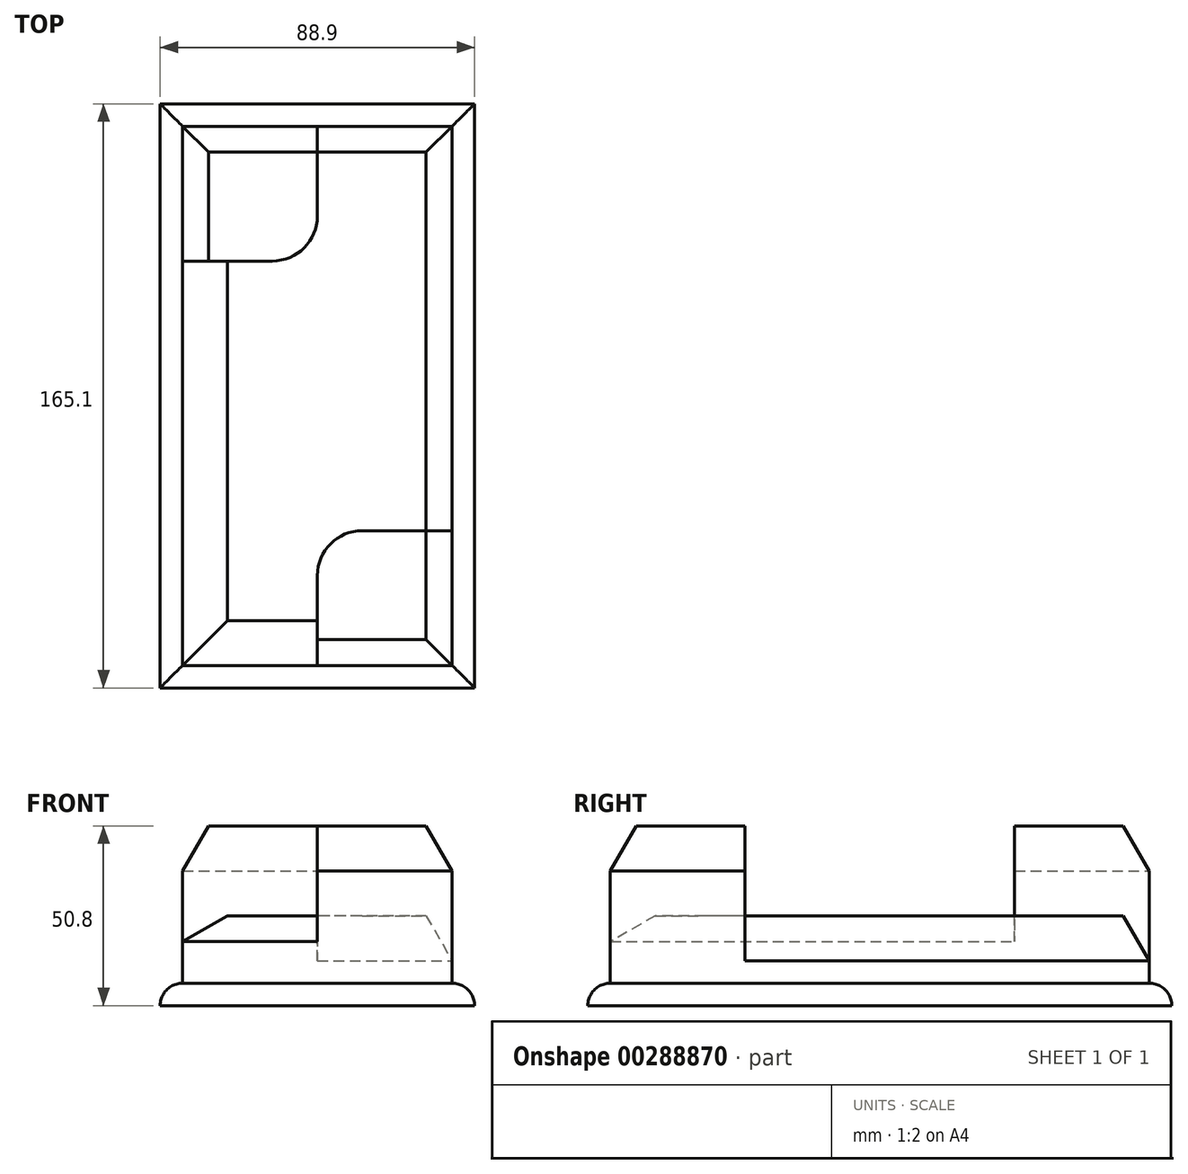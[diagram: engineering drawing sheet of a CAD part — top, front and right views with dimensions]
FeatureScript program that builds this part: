
annotation { "Feature Type Name" : "Feature", "Feature Type Description" : "" }
export const myFeature = defineFeature(function(context is Context, id is Id, definition is map)
    precondition{}
    {
        {
            var Q0;
            Q0=qCreatedBy(makeId("Top.planeOp"),FACE);
            var sketch = newSketch(context, id + "F0", { "sketchPlane" : qUnion([Q0])});
            skLineSegment(sketch, "E0.bottom", {"start": v(-58.88, 81.26) * mm, "end": v(30.02, 81.26) * mm});
            skLineSegment(sketch, "E0.top", {"start": v(-58.88, -83.84) * mm, "end": v(30.02, -83.84) * mm});
            skLineSegment(sketch, "E0.left", {"start": v(-58.88, 81.26) * mm, "end": v(-58.88, -83.84) * mm});
            skLineSegment(sketch, "E0.right", {"start": v(30.02, 81.26) * mm, "end": v(30.02, -83.84) * mm});
            skLineSegment(sketch, "E1.0", {"start": v(-52.53, 74.91) * mm, "end": v(23.67, 74.91) * mm});
            skLineSegment(sketch, "E1.1", {"start": v(-52.53, 74.91) * mm, "end": v(-52.53, -77.49) * mm});
            skLineSegment(sketch, "E1.2", {"start": v(-52.53, -77.49) * mm, "end": v(23.67, -77.49) * mm});
            skLineSegment(sketch, "E1.3", {"start": v(23.67, 74.91) * mm, "end": v(23.67, -77.49) * mm});
            skLineSegment(sketch, "E2", {"start": v(-14.43, 74.91) * mm, "end": v(-14.43, 49.51) * mm});
            skLineSegment(sketch, "E3", {"start": v(-27.13, 36.81) * mm, "end": v(-52.53, 36.81) * mm});
            skLineSegment(sketch, "E4", {"start": v(-14.43, -77.49) * mm, "end": v(-14.43, -52.09) * mm});
            skLineSegment(sketch, "E5", {"start": v(-1.73, -39.39) * mm, "end": v(23.67, -39.39) * mm});
            skPoint(sketch, "E6.visualSharp", {"position": v(-14.43, 36.81) * mm});
            skArc(sketch, "E6.filletArc", {"start": v(-27.13, 36.81) * mm, "mid": v(-18.15, 40.53) * mm, "end": v(-14.43, 49.51) * mm});
            skPoint(sketch, "E7.visualSharp", {"position": v(-14.43, -39.39) * mm});
            skArc(sketch, "E7.filletArc", {"start": v(-1.73, -39.39) * mm, "mid": v(-10.71, -43.1) * mm, "end": v(-14.43, -52.09) * mm});
            skSolve(sketch);
        }
        {
            var Q0;
            Q0=makeQuery(id+"F0.imprint","IMPRINT",FACE,{"disambiguationData":[TD([[makeQuery(id+"F0.imprint","IMPRINT",EDGE,{"derivedFrom":sQuery(id+"F0.wireOp",EDGE,"E0.bottom")}),-1.0]])]});
            extrude(context, id + "F1", {"entities" : qUnion([Q0]), "depth" : 6.35 * mm});
        }
        {
            var Q0;
            {var subQ9=sQuery(id+"F0.wireOp",EDGE,"E2");Q0=makeQuery(id+"F0.imprint","IMPRINT",FACE,{"disambiguationData":[TD([[makeQuery(id+"F0.imprint","IMPRINT",EDGE,{"derivedFrom":subQ9}),1.0]])]});}
            extrude(context, id + "F2", {"entities" : qUnion([Q0]), "operationType" : NewBodyOperationType.ADD, "depth" : 25.4 * mm});
        }
        {
            var Q0;
            {var subQ1=sQuery(id+"F0.wireOp",EDGE,"E2");Q0=makeQuery(id+"F0.imprint","IMPRINT",FACE,{"disambiguationData":[TD([[makeQuery(id+"F0.imprint","IMPRINT",EDGE,{"derivedFrom":subQ1}),-1.0]])]});}
            var Q1;
            {var subQ4=sQuery(id+"F0.wireOp",EDGE,"E4");Q1=makeQuery(id+"F0.imprint","IMPRINT",FACE,{"disambiguationData":[TD([[makeQuery(id+"F0.imprint","IMPRINT",EDGE,{"derivedFrom":subQ4}),-1.0]])]});}
            extrude(context, id + "F3", {"entities" : qUnion([Q0, Q1]), "operationType" : NewBodyOperationType.ADD, "depth" : 50.8 * mm});
        }
        {
            var Q0;
            Q0=makeQuery(id+"F1.opExtrude","CAP_EDGE",EDGE,{"disambiguationData":[OSD([sQuery(id+"F0.wireOp",EDGE,"E0.top")])],"isStart":false});
            var Q1;
            Q1=makeQuery(id+"F1.opExtrude","CAP_EDGE",EDGE,{"disambiguationData":[OSD([sQuery(id+"F0.wireOp",EDGE,"E0.bottom")])],"isStart":false});
            var Q2;
            Q2=makeQuery(id+"F1.opExtrude","CAP_EDGE",EDGE,{"disambiguationData":[OSD([sQuery(id+"F0.wireOp",EDGE,"E0.right")])],"isStart":false});
            var Q3;
            Q3=makeQuery(id+"F1.opExtrude","CAP_EDGE",EDGE,{"disambiguationData":[OSD([sQuery(id+"F0.wireOp",EDGE,"E0.left")])],"isStart":false});
            fillet(context, id + "F4", {"entities" : qUnion([Q0, Q1, Q2, Q3]), "radius" : 6.35 * mm, "tangentPropagation" : true, "allowEdgeOverflow" : false});
        }
        {
            var Q0;
            Q0=makeQuery(id+"F3.opExtrude","CAP_EDGE",EDGE,{"disambiguationData":[OSD([sQuery(id+"F0.wireOp",EDGE,"E1.0")])],"isStart":false});
            var Q1;
            Q1=makeQuery(id+"F3.opExtrude","CAP_EDGE",EDGE,{"disambiguationData":[OSD([sQuery(id+"F0.wireOp",EDGE,"E1.1")])],"isStart":false});
            var Q2;
            Q2=makeQuery(id+"F2.opExtrude","CAP_EDGE",EDGE,{"disambiguationData":[OSD([sQuery(id+"F0.wireOp",EDGE,"E1.3")])],"isStart":false});
            var Q3;
            Q3=makeQuery(id+"F2.opExtrude","CAP_EDGE",EDGE,{"disambiguationData":[OSD([sQuery(id+"F0.wireOp",EDGE,"E1.2")])],"isStart":false});
            var Q4;
            Q4=makeQuery(id+"F2.opExtrude","CAP_EDGE",EDGE,{"disambiguationData":[OSD([sQuery(id+"F0.wireOp",EDGE,"E1.1")])],"isStart":false});
            var Q5;
            Q5=makeQuery(id+"F2.opExtrude","CAP_EDGE",EDGE,{"disambiguationData":[OSD([sQuery(id+"F0.wireOp",EDGE,"E1.0")])],"isStart":false});
            chamfer(context, id + "F5", {"entities" : qUnion([Q0, Q1, Q2, Q3, Q4, Q5]), "chamferType" : ChamferType.OFFSET_ANGLE, "width" : 12.7 * mm, "oppositeDirection" : false, "angle" : 30 * degree, "tangentPropagation" : true});
        }
        {
            var Q0;
            Q0=makeQuery(id+"F3.opExtrude","CAP_EDGE",EDGE,{"disambiguationData":[OSD([sQuery(id+"F0.wireOp",EDGE,"E1.3")])],"isStart":false});
            var Q1;
            Q1=makeQuery(id+"F3.opExtrude","CAP_EDGE",EDGE,{"disambiguationData":[OSD([sQuery(id+"F0.wireOp",EDGE,"E1.2")])],"isStart":false});
            chamfer(context, id + "F6", {"entities" : qUnion([Q0, Q1]), "chamferType" : ChamferType.OFFSET_ANGLE, "width" : 12.7 * mm, "oppositeDirection" : false, "angle" : 30 * degree, "tangentPropagation" : true});
        }
    });
